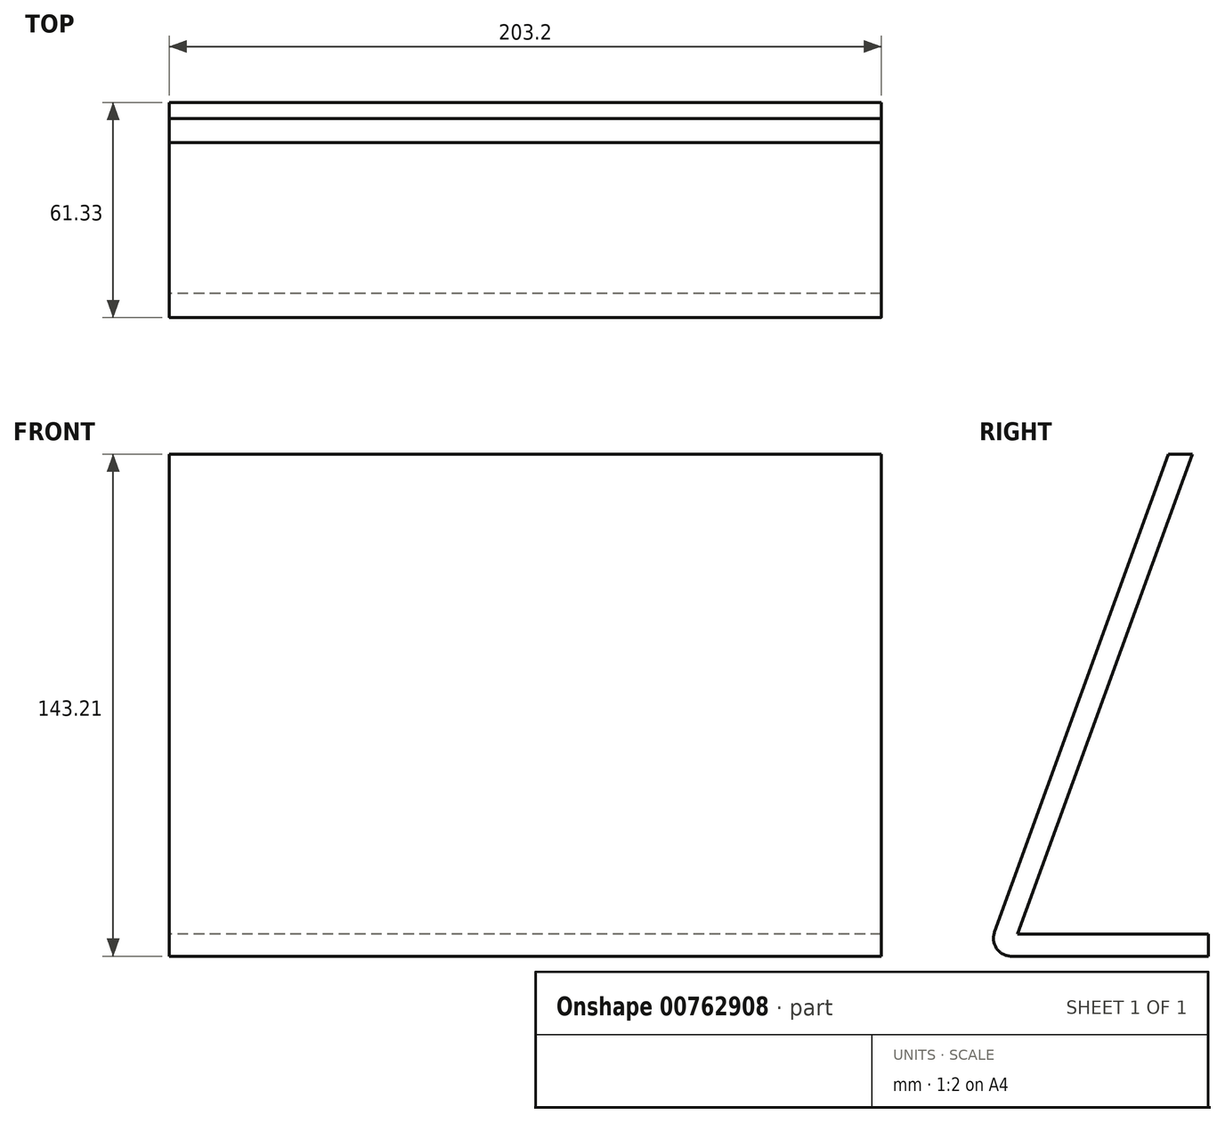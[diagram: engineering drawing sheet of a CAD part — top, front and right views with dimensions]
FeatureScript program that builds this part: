
annotation { "Feature Type Name" : "Feature", "Feature Type Description" : "" }
export const myFeature = defineFeature(function(context is Context, id is Id, definition is map)
    precondition{}
    {
        {
            var Q0;
            Q0=qCreatedBy(makeId("Right.planeOp"),FACE);
            var sketch = newSketch(context, id + "F0", { "sketchPlane" : qUnion([Q0])});
            skLineSegment(sketch, "E0", {"start": v(0, 0) * mm, "end": v(52.12, 143.2) * mm});
            skLineSegment(sketch, "E1", {"start": v(0, 0) * mm, "end": v(63.5, 0) * mm});
            skLineSegment(sketch, "E2.0", {"start": v(9.07, 6.35) * mm, "end": v(58.88, 143.2) * mm});
            skLineSegment(sketch, "E2.1", {"start": v(9.07, 6.35) * mm, "end": v(63.5, 6.35) * mm});
            skLineSegment(sketch, "E3", {"start": v(52.12, 143.2) * mm, "end": v(58.88, 143.2) * mm});
            skLineSegment(sketch, "E4", {"start": v(63.5, 6.35) * mm, "end": v(63.5, 0) * mm});
            skSolve(sketch);
        }
        {
            var Q0;
            Q0=makeQuery(id+"F0.imprint","IMPRINT",FACE,{"disambiguationData":[TD([[makeQuery(id+"F0.imprint","IMPRINT",EDGE,{"derivedFrom":sQuery(id+"F0.wireOp",EDGE,"E0")}),-1.0]])]});
            extrude(context, id + "F1", {"entities" : qUnion([Q0]), "depth" : 203.2 * mm, "offsetDistance" : 25.4 * mm, "symmetric" : true});
        }
        {
            var Q0;
            Q0=makeQuery(id+"F1.opExtrude","SWEPT_EDGE",EDGE,{"disambiguationData":[OSD([sQuery(id+"F0.wireOp",EDGE,"E0"),sQuery(id+"F0.wireOp",EDGE,"E1")])]});
            fillet(context, id + "F2", {"entities" : qUnion([Q0]), "radius" : 5.08 * mm, "tangentPropagation" : true, "allowEdgeOverflow" : false});
        }
    });
